# Revit family: Building-ContenitoriParete-GEWISS-44CE-CASSETTE-DERIVAZIONE-PARETE_14FORI
name_source: partatom
category: Apparecchi elettrici
revit_build: Autodesk Revit 2016 (Build: 20161004_0715(x64)
units: mm (PartAtom-declared; Revit-internal decimal feet)

## family parameters
Condiviso = No
Host = Superficie
Mantenere orientamento annotazione = Sì
Numero OmniClass = 23.80.30.14.24
Punto di calcolo locali = Sì
Quota connettore circolare = Usa diametro
Taglio con vuoti quando caricato = No
Tipo di parte = Normale
Titolo OmniClass = Junction Boxes

## types (1)
- Building-ContenitoriParete-GEWISS-44CE-CASSETTE-DERIVAZIONE-PARETE_14FORI
    Accessori per ripristino isolamento = GW44621
    Applicazione = Derivazioni speciali
    Carico apparente = 0 VA
    Catalogo = BUILDING
    Catalogo Serie = 44 CE
    Classe isolamento = II (secondo Norma IEC 61140)
    Classificazione = Other
    Codice EAN = 8011564243866
    Codice Electrocod = 02210
    Colore = Grigio RAL 7035
    Coperchio = Basso a vite
    Coperchio_ = <Per categoria>
    Coppia serraggio viti = 1,8NM
    Descrizione = CASS.IP55 460X380X120 PASS.GWT 960°C
    Diametro ingresso corugato = 40 mm  [stored 0.131234 ft]
    Dim. interne BxHxP (mm) = 460x380x120
    Entrate N. fori / Ã˜ = 14 / 48
    Glow Wire Test = 960°C
    Grado di protezione = IP55
    IDF = c8c44e86-0ca7-4378-9988-4ca5ba28cc68
    IDT = 1bef6471-8e2d-4dfc-87b3-9fc971884851
    Immagine tipo = GW44061.jpg
    Larghezza_interna = 460 mm  [stored 1.50919 ft]
    Lunghezza_interna = 380 mm
    Materiale = Tecnopolimero GWPLAST 75
    Modello = GW44061
    Numero di poli = 3
    Pareti = Con passacavi
    Produttore = GEWISS S.p.A.
    Prospetto di default = 1219 mm
    Raggio = 20 mm  [stored 0.0656168 ft]
    Resistenza agli urti = IK08
    SEO = Cassetta
    Scatola_ = <Per categoria>
    Scheda Tecnica = https://www.gewiss.com
    Spessore = 120 mm  [stored 0.393701 ft]
    Temperatura di impiego = -25 +60 °C
    Termopressione con biglia = 85 °C
    URL = https://www.gewiss.com
    Versione file RFA = 18.0
    Viti coperchio (n. e Tipo) = 4 isol. a cerniera piombabili
    Voltaggio_x = 0 V

note: [stored X ft] marks values corroborated as IEEE doubles in the binary element streams (Revit-internal decimal feet)

## geometry (parser evidence)
native form markers: Blend x2, Sweep x2
no freeform markers — native parametric forms only
